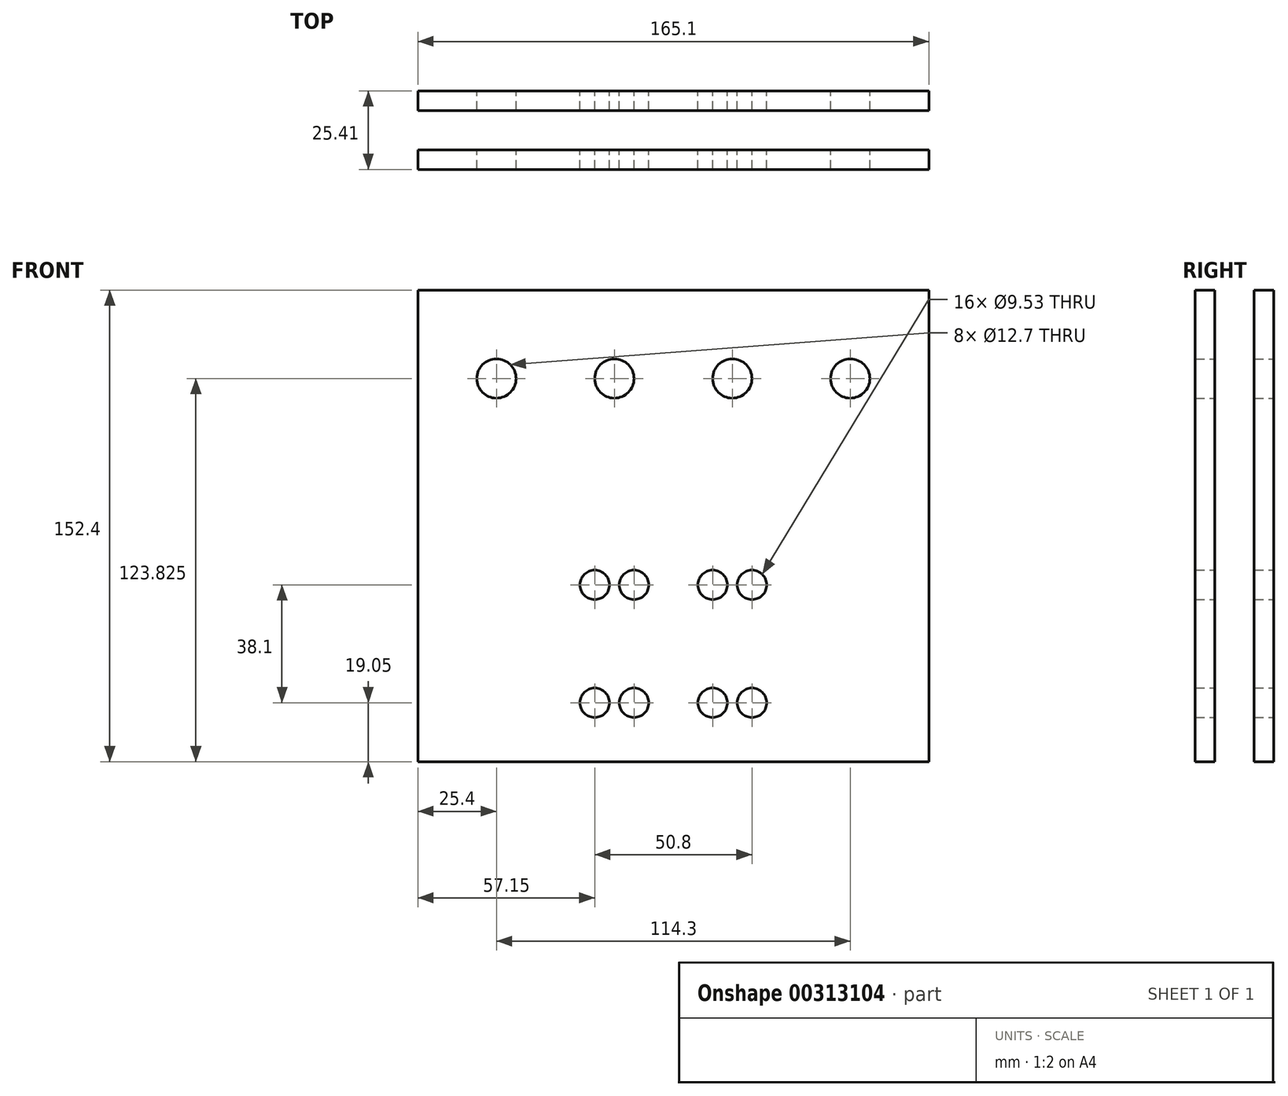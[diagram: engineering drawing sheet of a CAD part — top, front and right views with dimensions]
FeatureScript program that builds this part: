
annotation { "Feature Type Name" : "Feature", "Feature Type Description" : "" }
export const myFeature = defineFeature(function(context is Context, id is Id, definition is map)
    precondition{}
    {
        {
            var Q0;
            Q0=qCreatedBy(makeId("Top.planeOp"),FACE);
            var sketch = newSketch(context, id + "F0", { "sketchPlane" : qUnion([Q0])});
            skLineSegment(sketch, "E0.bottom", {"start": v(82.55, 3.18) * mm, "end": v(-82.55, 3.18) * mm});
            skLineSegment(sketch, "E0.top", {"start": v(82.55, -3.18) * mm, "end": v(-82.55, -3.18) * mm});
            skLineSegment(sketch, "E0.left", {"start": v(82.55, 3.18) * mm, "end": v(82.55, -3.18) * mm});
            skLineSegment(sketch, "E0.right", {"start": v(-82.55, 3.18) * mm, "end": v(-82.55, -3.18) * mm});
            skPoint(sketch, "E0.middle", {"position": v(0, 0) * mm});
            skLineSegment(sketch, "E1.bottom", {"start": v(82.55, -15.88) * mm, "end": v(-82.55, -15.88) * mm});
            skLineSegment(sketch, "E1.top", {"start": v(82.55, -22.23) * mm, "end": v(-82.55, -22.23) * mm});
            skLineSegment(sketch, "E1.left", {"start": v(82.55, -15.88) * mm, "end": v(82.55, -22.23) * mm});
            skLineSegment(sketch, "E1.right", {"start": v(-82.55, -15.88) * mm, "end": v(-82.55, -22.23) * mm});
            skPoint(sketch, "E1.middle", {"position": v(0, -19.05) * mm});
            skSolve(sketch);
        }
        {
            var Q0;
            Q0 = qSketchRegion(id + "F0", true);
            extrude(context, id + "F1", {"entities" : qUnion([Q0]), "endBound" : BoundingType.SYMMETRIC, "depth" : 152.4 * mm});
        }
        {
            var Q0;
            Q0=makeQuery(id+"F1.opExtrude","SWEPT_FACE",FACE,{"disambiguationData":[OSD([sQuery(id+"F0.wireOp",EDGE,"E0.bottom")])]});
            var sketch = newSketch(context, id + "F2", { "sketchPlane" : qUnion([Q0])});
            skCircle(sketch, "E2", {"center": v(-12.7, -57.15) * mm, "radius": 4.76 * mm});
            skCircle(sketch, "E3", {"center": v(25.4, -57.15) * mm, "radius": 4.76 * mm});
            skCircle(sketch, "E4", {"center": v(25.4, -19.05) * mm, "radius": 4.76 * mm});
            skCircle(sketch, "E5", {"center": v(-12.7, -19.05) * mm, "radius": 4.76 * mm});
            skCircle(sketch, "E6", {"center": v(-57.15, 47.62) * mm, "radius": 6.35 * mm});
            skCircle(sketch, "E7.1.0.0", {"center": v(-19.05, 47.62) * mm, "radius": 6.35 * mm});
            skCircle(sketch, "E7.2.0.0", {"center": v(19.05, 47.63) * mm, "radius": 6.35 * mm});
            skCircle(sketch, "E7.3.0.0", {"center": v(57.15, 47.63) * mm, "radius": 6.35 * mm});
            skLineSegment(sketch, "E7.direction1", {"start": v(-57.15, 47.62) * mm, "end": v(-19.05, 47.62) * mm, "construction": true});
            skLineSegment(sketch, "E8", {"start": v(-12.7, -57.15) * mm, "end": v(25.4, -57.15) * mm, "construction": true});
            skPoint(sketch, "E9", {"position": v(6.35, -57.15) * mm});
            skPoint(sketch, "E10.1.0.0", {"position": v(-6.35, -57.15) * mm});
            skLineSegment(sketch, "E10.1.0.1", {"start": v(-25.4, -57.15) * mm, "end": v(12.7, -57.15) * mm, "construction": true});
            skCircle(sketch, "E10.1.0.2", {"center": v(-25.4, -19.05) * mm, "radius": 4.76 * mm});
            skCircle(sketch, "E10.1.0.3", {"center": v(12.7, -19.05) * mm, "radius": 4.76 * mm});
            skCircle(sketch, "E10.1.0.4", {"center": v(12.7, -57.15) * mm, "radius": 4.76 * mm});
            skCircle(sketch, "E10.1.0.5", {"center": v(-25.4, -57.15) * mm, "radius": 4.76 * mm});
            skLineSegment(sketch, "E10.direction1", {"start": v(-12.7, -57.15) * mm, "end": v(-25.4, -57.15) * mm, "construction": true});
            skSolve(sketch);
        }
        {
            var Q0;
            Q0 = qSketchRegion(id + "F2", true);
            extrude(context, id + "F3", {"entities" : qUnion([Q0]), "operationType" : NewBodyOperationType.REMOVE, "endBound" : BoundingType.THROUGH_ALL, "oppositeDirection" : true, "depth" : 25.4 * mm});
        }
    });
